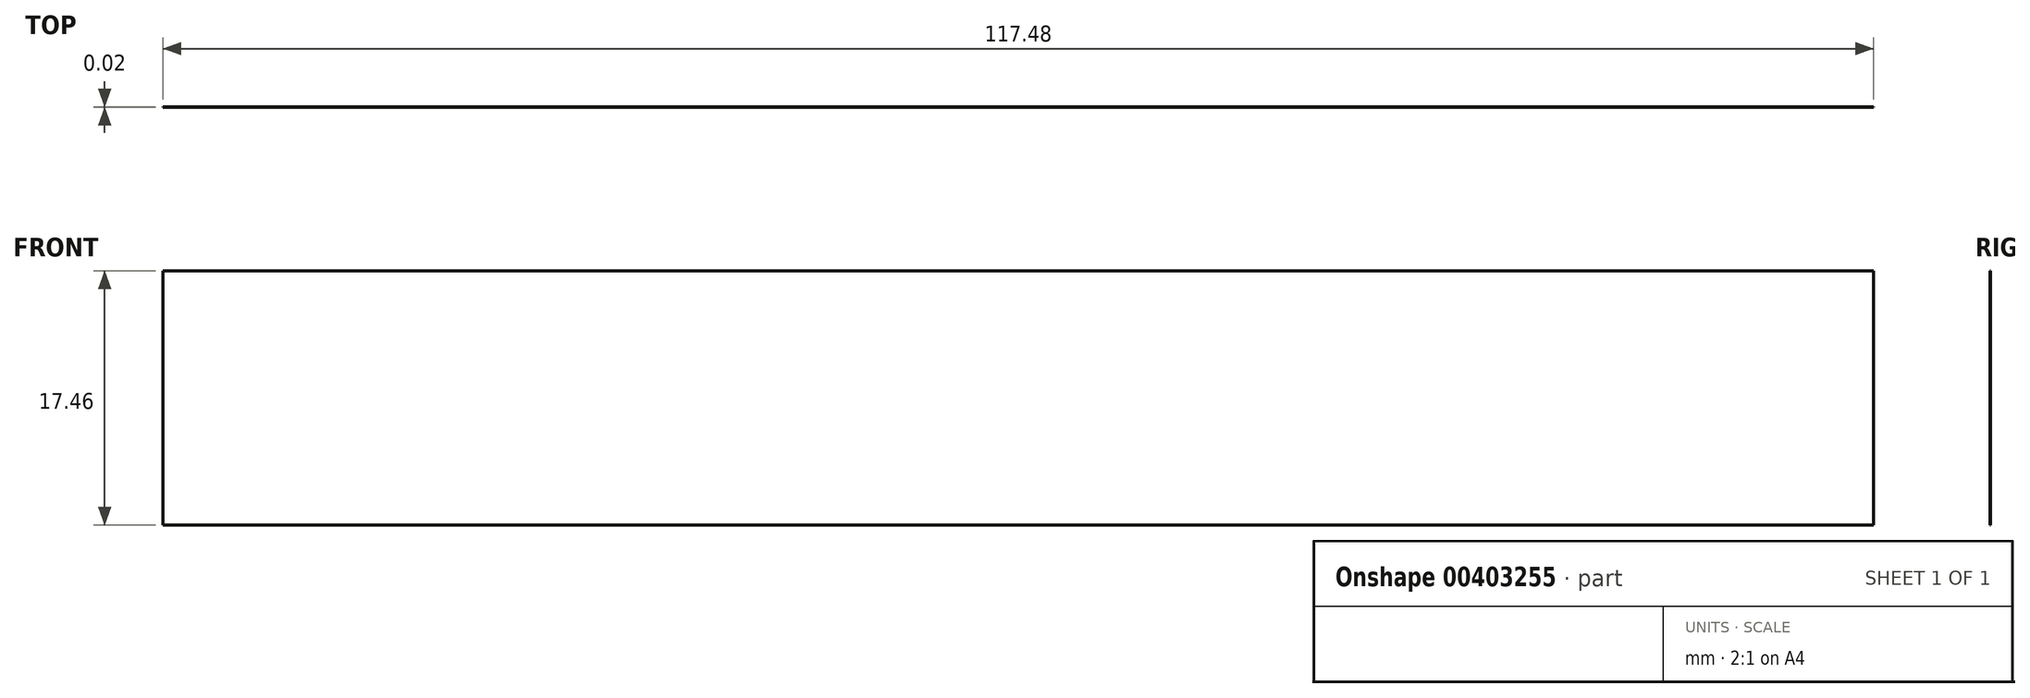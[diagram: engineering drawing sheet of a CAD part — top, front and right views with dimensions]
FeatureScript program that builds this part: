
annotation { "Feature Type Name" : "Feature", "Feature Type Description" : "" }
export const myFeature = defineFeature(function(context is Context, id is Id, definition is map)
    precondition{}
    {
        {
            var Q0;
            Q0=qCreatedBy(makeId("Front.planeOp"),FACE);
            var sketch = newSketch(context, id + "F0", { "sketchPlane" : qUnion([Q0])});
            skLineSegment(sketch, "E0.bottom", {"start": v(-58.74, 8.73) * mm, "end": v(58.74, 8.73) * mm});
            skLineSegment(sketch, "E0.top", {"start": v(-58.74, -8.73) * mm, "end": v(58.74, -8.73) * mm});
            skLineSegment(sketch, "E0.left", {"start": v(-58.74, 8.73) * mm, "end": v(-58.74, -8.73) * mm});
            skLineSegment(sketch, "E0.right", {"start": v(58.74, 8.73) * mm, "end": v(58.74, -8.73) * mm});
            skSolve(sketch);
        }
        {
            var Q0;
            Q0=makeQuery(id+"F0.imprint","IMPRINT",FACE,{"disambiguationData":[TD([[makeQuery(id+"F0.imprint","IMPRINT",EDGE,{"derivedFrom":sQuery(id+"F0.wireOp",EDGE,"E0.bottom")}),-1.0]])]});
            extrude(context, id + "F1", {"entities" : qUnion([Q0]), "endBound" : BoundingType.SYMMETRIC, "depth" : 11 / 406.4 * mm});
        }
    });
